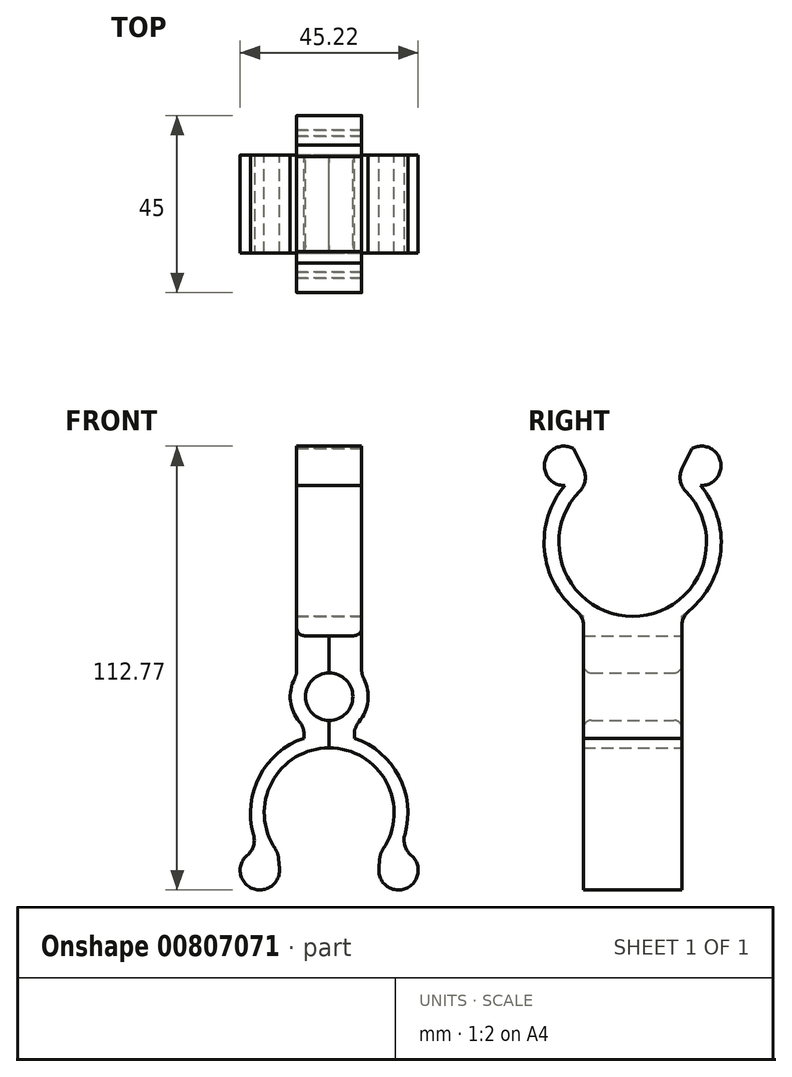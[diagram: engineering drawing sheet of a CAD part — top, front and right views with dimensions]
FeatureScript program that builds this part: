
annotation { "Feature Type Name" : "Feature", "Feature Type Description" : "" }
export const myFeature = defineFeature(function(context is Context, id is Id, definition is map)
    precondition{}
    {
        {
            var Q0;
            Q0=qCreatedBy(makeId("Front.planeOp"),FACE);
            var sketch = newSketch(context, id + "F0", { "sketchPlane" : qUnion([Q0])});
            skLineSegment(sketch, "E0", {"start": v(12.97, -39.72) * mm, "end": v(12.63, -43.7) * mm});
            skArc(sketch, "E1", {"start": v(12.63, -43.7) * mm, "mid": v(21.02, -47.8) * mm, "end": v(17.54, -39.13) * mm});
            skArc(sketch, "E2", {"start": v(6.38, -7.57) * mm, "mid": v(9.8, -1.4) * mm, "end": v(8.25, 5.48) * mm});
            skArc(sketch, "E3", {"start": v(0, -6.02) * mm, "mid": v(6.02, 0) * mm, "end": v(0, 6.02) * mm});
            skPoint(sketch, "E4.end.orphan", {"position": v(8.25, 0) * mm});
            skLineSegment(sketch, "E5", {"start": v(0, 71.13) * mm, "end": v(0, -72.93) * mm, "construction": true});
            skLineSegment(sketch, "E6", {"start": v(8.25, 5.48) * mm, "end": v(8.25, 15.48) * mm});
            skLineSegment(sketch, "E7", {"start": v(0.13, 84.1) * mm, "end": v(0, 71.13) * mm, "construction": true});
            skLineSegment(sketch, "E8", {"start": v(8.25, 15.48) * mm, "end": v(0, 15.48) * mm});
            skLineSegment(sketch, "E9", {"start": v(0, 15.48) * mm, "end": v(0, 6.02) * mm});
            skLineSegment(sketch, "E10", {"start": v(0, -6.02) * mm, "end": v(0, -29.52) * mm});
            skArc(sketch, "E11", {"start": v(12.97, -39.72) * mm, "mid": v(14.84, -22.31) * mm, "end": v(0, -13.02) * mm});
            skLineSegment(sketch, "E12", {"start": v(6.38, -7.57) * mm, "end": v(6.38, -10.57) * mm});
            skArc(sketch, "E13", {"start": v(17.54, -39.13) * mm, "mid": v(18.63, -22.25) * mm, "end": v(6.38, -10.57) * mm});
            skSolve(sketch);
        }
        {
            var Q0;
            Q0 = qSketchRegion(id + "F0", true);
            extrude(context, id + "F1", {"entities" : qUnion([Q0]), "depth" : 25 * mm, "offsetDistance" : 25 * mm});
        }
        {
            var Q0;
            Q0=makeQuery(id+"F1.opExtrude","SWEPT_FACE",FACE,{"disambiguationData":[OSD([sQuery(id+"F0.wireOp",EDGE,"E6")])]});
            var sketch = newSketch(context, id + "F2", { "sketchPlane" : qUnion([Q0])});
            skLineSegment(sketch, "E14", {"start": v(-12.5, 20.4) * mm, "end": v(-12.5, 67.62) * mm, "construction": true});
            skPoint(sketch, "E15.end.orphan", {"position": v(-12.5, 15.48) * mm});
            skArc(sketch, "E16", {"start": v(-23.35, 54.45) * mm, "mid": v(-12.5, 20.4) * mm, "end": v(-1.65, 54.45) * mm});
            skArc(sketch, "E17", {"start": v(0, 20.45) * mm, "mid": v(9.78, 36) * mm, "end": v(4.71, 53.65) * mm});
            skLineSegment(sketch, "E18.trimOffspring", {"start": v(-25, 20.45) * mm, "end": v(-25, 15.48) * mm});
            skLineSegment(sketch, "E19.trimOffspring", {"start": v(0, 20.45) * mm, "end": v(0, 15.48) * mm});
            skPoint(sketch, "E20.MirrorCS.start.orphan", {"position": v(0, 31.6) * mm});
            skPoint(sketch, "E21.orphan", {"position": v(-12.5, 19.02) * mm});
            skArc(sketch, "E22.trimOffspring", {"start": v(-25, 57.87) * mm, "mid": v(-25, 57.86) * mm, "end": v(-25, 57.86) * mm});
            skArc(sketch, "E23", {"start": v(0, 57.87) * mm, "mid": v(0, 57.86) * mm, "end": v(0, 57.85) * mm});
            skArc(sketch, "E24.MirrorCS", {"start": v(-25, 57.87) * mm, "mid": v(-25, 57.86) * mm, "end": v(-25, 57.85) * mm});
            skLineSegment(sketch, "E25", {"start": v(-27.5, 63) * mm, "end": v(-23.35, 54.45) * mm});
            skPoint(sketch, "E26.MirrorCS.start.orphan", {"position": v(-27.5, 63) * mm});
            skLineSegment(sketch, "E27.MirrorCS", {"start": v(2.5, 63) * mm, "end": v(-1.65, 54.45) * mm});
            skArc(sketch, "E28.trimOffspring", {"start": v(4.71, 53.65) * mm, "mid": v(9.8, 59.8) * mm, "end": v(2.5, 63) * mm});
            skArc(sketch, "E29.trimOffspring", {"start": v(0, 57.86) * mm, "mid": v(0, 57.86) * mm, "end": v(0, 57.87) * mm});
            skArc(sketch, "E30.trimOffspring", {"start": v(-29.71, 53.65) * mm, "mid": v(-34.8, 59.8) * mm, "end": v(-27.5, 63) * mm});
            skArc(sketch, "E31.trimOffspring", {"start": v(-29.71, 53.65) * mm, "mid": v(-34.78, 36) * mm, "end": v(-25, 20.45) * mm});
            skSolve(sketch);
        }
        {
            var Q0;
            Q0=makeQuery(id+"F2.imprint","IMPRINT",FACE,{"disambiguationData":[TD([[makeQuery(id+"F2.imprint","IMPRINT",EDGE,{"derivedFrom":sQuery(id+"F2.wireOp",EDGE,"E16")}),-1.0]])]});
            extrude(context, id + "F3", {"entities" : qUnion([Q0]), "operationType" : NewBodyOperationType.ADD, "oppositeDirection" : true, "depth" : 16.5 * mm, "offsetDistance" : 25 * mm});
        }
        {
            var Q0;
            Q0=makeQuery(id+"F1.opExtrude","SWEPT_BODY",BODY,{"disambiguationData":[OSD([sQuery(id+"F0.wireOp",EDGE,"cfabb739-dba9-4975-bd49-091e3b57f569"),sQuery(id+"F0.wireOp",EDGE,"5847780e-0f5a-4472-9120-1fdb006a39dd"),sQuery(id+"F0.wireOp",EDGE,"E0"),sQuery(id+"F0.wireOp",EDGE,"E1"),sQuery(id+"F0.wireOp",EDGE,"E2"),sQuery(id+"F0.wireOp",EDGE,"E3"),sQuery(id+"F0.wireOp",EDGE,"LwMaPAxc-ASng-TWKL-FKsP-XUbiFX4LCitD"),sQuery(id+"F0.wireOp",EDGE,"E6"),sQuery(id+"F0.wireOp",EDGE,"E8"),sQuery(id+"F0.wireOp",EDGE,"E9"),sQuery(id+"F0.wireOp",EDGE,"E10")])]});
            var Q1;
            Q1=qCreatedBy(makeId("Right.planeOp"),FACE);
            mirror(context, id + "F4", {"entities" : qUnion([Q0]), "mirrorPlane" : qUnion([Q1])});
        }
        {
            var Q0;
            Q0=makeQuery(id+"F1.opExtrude","SWEPT_EDGE",EDGE,{"disambiguationData":[OSD([sQuery(id+"F0.wireOp",EDGE,"E0"),sQuery(id+"F0.wireOp",EDGE,"E11")])]});
            var Q1;
            Q1=makeQuery(id+"F4.opPattern","COPY",EDGE,{"derivedFrom":makeQuery(id+"F1.opExtrude","SWEPT_EDGE",EDGE,{"disambiguationData":[OSD([sQuery(id+"F0.wireOp",EDGE,"E0"),sQuery(id+"F0.wireOp",EDGE,"E11")])]}),"instanceName":"1"});
            var Q2;
            Q2=makeQuery(id+"F4.opPattern","COPY",EDGE,{"derivedFrom":makeQuery(id+"F1.opExtrude","SWEPT_EDGE",EDGE,{"disambiguationData":[OSD([sQuery(id+"F0.wireOp",EDGE,"E1"),sQuery(id+"F0.wireOp",EDGE,"E13")])]}),"instanceName":"1"});
            var Q3;
            Q3=makeQuery(id+"F1.opExtrude","SWEPT_EDGE",EDGE,{"disambiguationData":[OSD([sQuery(id+"F0.wireOp",EDGE,"E1"),sQuery(id+"F0.wireOp",EDGE,"E13")])]});
            var Q4;
            Q4=makeQuery(id+"F4.opPattern","COPY",EDGE,{"derivedFrom":makeQuery(id+"F1.opExtrude","SWEPT_EDGE",EDGE,{"disambiguationData":[OSD([sQuery(id+"F0.wireOp",EDGE,"E2"),sQuery(id+"F0.wireOp",EDGE,"E6")])]}),"instanceName":"1"});
            var Q5;
            Q5=makeQuery(id+"F4.opPattern","COPY",EDGE,{"derivedFrom":makeQuery(id+"F1.opExtrude","SWEPT_EDGE",EDGE,{"disambiguationData":[OSD([sQuery(id+"F0.wireOp",EDGE,"E2"),sQuery(id+"F0.wireOp",EDGE,"E12")])]}),"instanceName":"1"});
            var Q6;
            Q6=makeQuery(id+"F1.opExtrude","SWEPT_EDGE",EDGE,{"disambiguationData":[OSD([sQuery(id+"F0.wireOp",EDGE,"E2"),sQuery(id+"F0.wireOp",EDGE,"E6")])]});
            var Q7;
            Q7=makeQuery(id+"F1.opExtrude","SWEPT_EDGE",EDGE,{"disambiguationData":[OSD([sQuery(id+"F0.wireOp",EDGE,"E2"),sQuery(id+"F0.wireOp",EDGE,"E12")])]});
            var Q8;
            Q8=makeQuery(id+"F4.opPattern","COPY",EDGE,{"derivedFrom":makeQuery(id+"F3.opExtrude","SWEPT_EDGE",EDGE,{"disambiguationData":[OSD([sQuery(id+"F2.wireOp",EDGE,"E17"),sQuery(id+"F2.wireOp",EDGE,"E19.trimOffspring")])]}),"instanceName":"1"});
            var Q9;
            Q9=makeQuery(id+"F4.opPattern","COPY",EDGE,{"derivedFrom":makeQuery(id+"F3.opExtrude","SWEPT_EDGE",EDGE,{"disambiguationData":[OSD([sQuery(id+"F2.wireOp",EDGE,"E18.trimOffspring"),sQuery(id+"F2.wireOp",EDGE,"E22.trimOffspring")])]}),"instanceName":"1"});
            var Q10;
            Q10=makeQuery(id+"F4.opPattern","COPY",EDGE,{"derivedFrom":makeQuery(id+"F3.opExtrude","SWEPT_EDGE",EDGE,{"disambiguationData":[OSD([sQuery(id+"F2.wireOp",EDGE,"E16"),sQuery(id+"F2.wireOp",EDGE,"E26.MirrorCS")])]}),"instanceName":"1"});
            var Q11;
            Q11=makeQuery(id+"F3.opExtrude","SWEPT_EDGE",EDGE,{"disambiguationData":[OSD([sQuery(id+"F2.wireOp",EDGE,"E16"),sQuery(id+"F2.wireOp",EDGE,"o45zF1qc-RgXT-cvMq-ReTE-ZHE0aTBPM8XX")])]});
            fillet(context, id + "F5", {"entities" : qUnion([Q0, Q1, Q2, Q3, Q4, Q5, Q6, Q7, Q8, Q9, Q10, Q11]), "radius" : 5 * mm, "tangentPropagation" : true, "allowEdgeOverflow" : false});
        }
        {
            var Q0;
            Q0=makeQuery(id+"F1.opExtrude","CAP_EDGE",EDGE,{"disambiguationData":[OSD([sQuery(id+"F0.wireOp",EDGE,"E3")])],"isStart":false});
            var Q1;
            Q1=makeQuery(id+"F4.opPattern","COPY",EDGE,{"derivedFrom":makeQuery(id+"F1.opExtrude","CAP_EDGE",EDGE,{"disambiguationData":[OSD([sQuery(id+"F0.wireOp",EDGE,"E3")])],"isStart":false}),"instanceName":"1"});
            var Q2;
            Q2=makeQuery(id+"F4.opPattern","COPY",EDGE,{"derivedFrom":makeQuery(id+"F1.opExtrude","CAP_EDGE",EDGE,{"disambiguationData":[OSD([sQuery(id+"F0.wireOp",EDGE,"E3")])],"isStart":true}),"instanceName":"1"});
            var Q3;
            Q3=makeQuery(id+"F1.opExtrude","CAP_EDGE",EDGE,{"disambiguationData":[OSD([sQuery(id+"F0.wireOp",EDGE,"E3")])],"isStart":true});
            var Q4;
            Q4=makeQuery(id+"F4.opPattern","COPY",EDGE,{"derivedFrom":makeQuery(id+"F3.opExtrude","CAP_EDGE",EDGE,{"disambiguationData":[OSD([sQuery(id+"F0.wireOp",EDGE,"E6"),sQuery(id+"F0.wireOp",EDGE,"E8")])],"isStart":false}),"instanceName":"1"});
            var Q5;
            Q5=makeQuery(id+"F3.opExtrude","CAP_EDGE",EDGE,{"disambiguationData":[OSD([sQuery(id+"F0.wireOp",EDGE,"E6"),sQuery(id+"F0.wireOp",EDGE,"E8")])],"isStart":false});
            fillet(context, id + "F6", {"entities" : qUnion([Q0, Q1, Q2, Q3, Q4, Q5]), "radius" : 2 * mm, "tangentPropagation" : true, "allowEdgeOverflow" : false});
        }
    });
